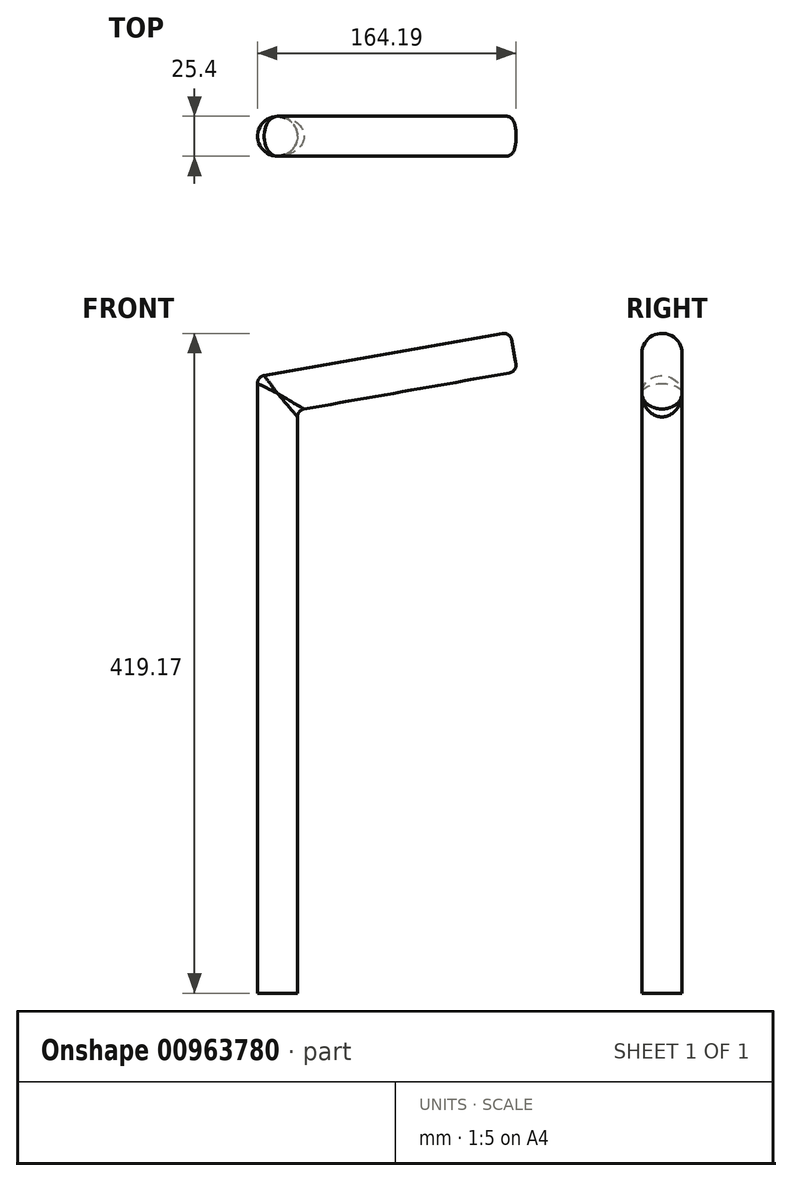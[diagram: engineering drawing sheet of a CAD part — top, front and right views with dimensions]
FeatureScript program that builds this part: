
annotation { "Feature Type Name" : "Feature", "Feature Type Description" : "" }
export const myFeature = defineFeature(function(context is Context, id is Id, definition is map)
    precondition{}
    {
        {
            var Q0;
            Q0=qCreatedBy(makeId("Front.planeOp"),FACE);
            var sketch = newSketch(context, id + "F0", { "sketchPlane" : qUnion([Q0])});
            skLineSegment(sketch, "E0", {"start": v(0, 0) * mm, "end": v(0, 381) * mm});
            skLineSegment(sketch, "E1", {"start": v(0, 381) * mm, "end": v(150.08, 407.46) * mm});
            skSolve(sketch);
        }
        {
            var Q0;
            Q0=qCreatedBy(makeId("Top.planeOp"),FACE);
            var sketch = newSketch(context, id + "F1", { "sketchPlane" : qUnion([Q0])});
            skCircle(sketch, "E2", {"center": v(0, 0) * mm, "radius": 12.7 * mm});
            skSolve(sketch);
        }
        {
            var Q0;
            Q0=makeQuery(id+"F1.imprint","IMPRINT",FACE,{"disambiguationData":[TD([[makeQuery(id+"F1.imprint","IMPRINT",EDGE,{"derivedFrom":sQuery(id+"F1.wireOp",EDGE,"E2")}),1.0]])]});
            var Q1;
            Q1=sQuery(id+"F0.wireOp",EDGE,"E0");
            var Q2;
            Q2=sQuery(id+"F0.wireOp",EDGE,"E1");
            sweep(context, id + "F2", {"profiles" : qUnion([Q0]), "path" : qUnion([Q1, Q2])});
        }
        {
            var Q0;
            Q0=makeQuery(id+"F2.opSweep","CAP_EDGE",EDGE,{"disambiguationData":[OSD([sQuery(id+"F0.wireOp",VERTEX,"E1.end"),sQuery(id+"F1.wireOp",EDGE,"E2")])],"isStart":false});
            var Q1;
            Q1=makeQuery(id+"F2.opSweep","MID_CAP_EDGE",EDGE,{"disambiguationData":[OSD([sQuery(id+"F0.wireOp",VERTEX,"E1.start"),sQuery(id+"F1.wireOp",EDGE,"E2")])],"capPos":1.0});
            fillet(context, id + "F3", {"entities" : qUnion([Q0, Q1]), "radius" : 5.08 * mm, "tangentPropagation" : true, "allowEdgeOverflow" : false});
        }
    });
